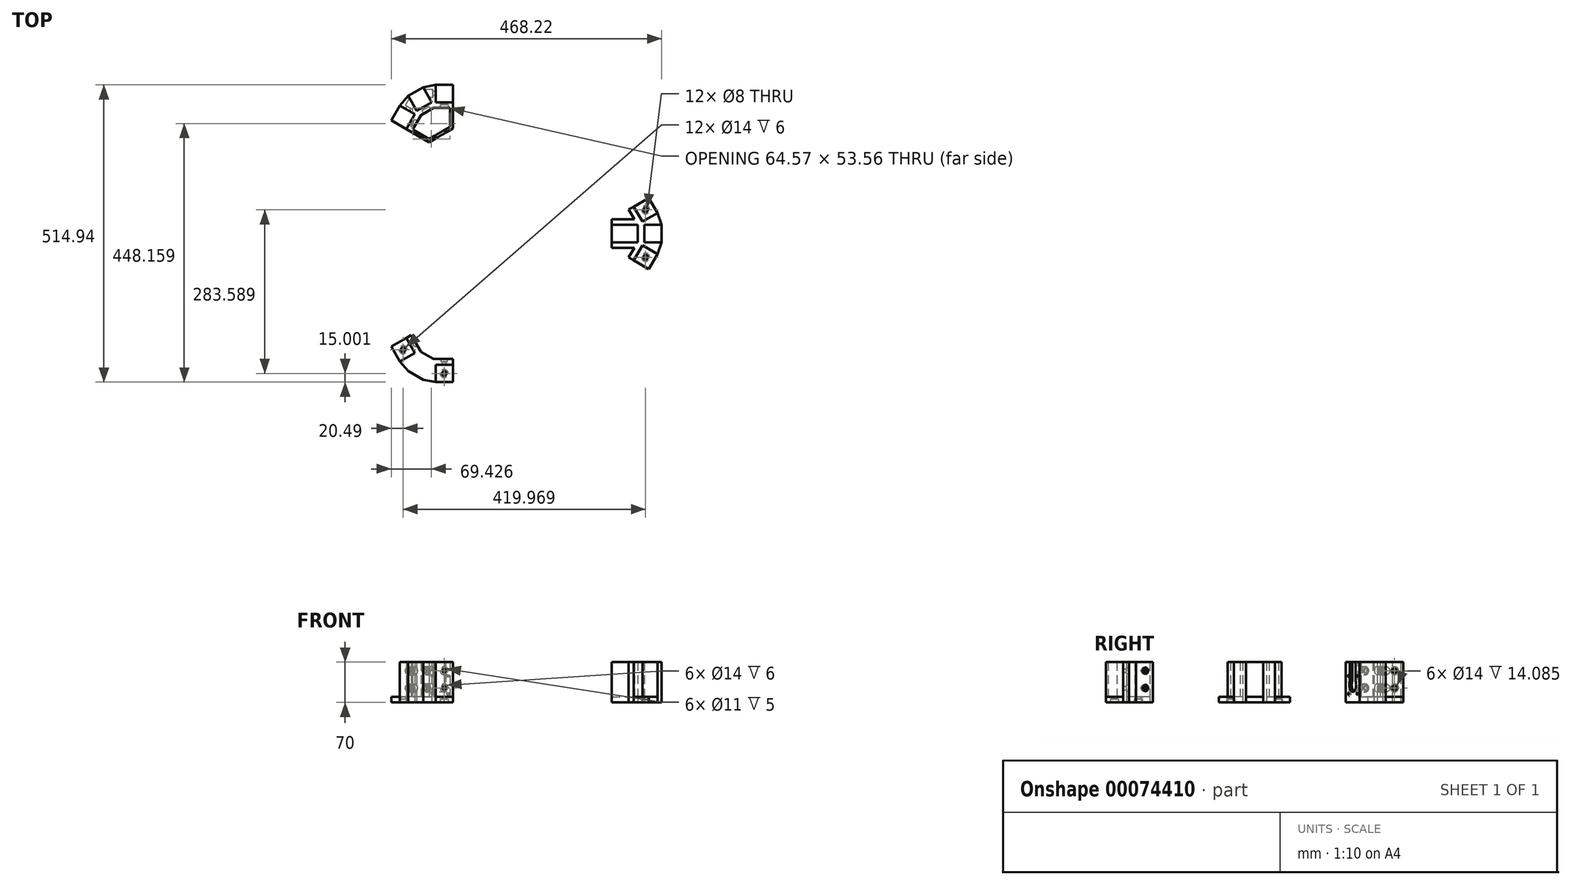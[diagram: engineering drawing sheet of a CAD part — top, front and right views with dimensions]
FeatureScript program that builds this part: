
annotation { "Feature Type Name" : "Feature", "Feature Type Description" : "" }
export const myFeature = defineFeature(function(context is Context, id is Id, definition is map)
    precondition{}
    {
        {
            var Q0;
            Q0=qCreatedBy(makeId("Top.planeOp"),FACE);
            var sketch = newSketch(context, id + "F0", { "sketchPlane" : qUnion([Q0])});
            skCircle(sketch, "E0", {"center": v(0, 0) * mm, "radius": 150 * mm, "construction": true});
            skCircle(sketch, "E1.cCircle", {"center": v(0, 0) * mm, "radius": 253.45 * mm, "construction": true});
            skLineSegment(sketch, "E1.0", {"start": v(-146.33, 253.45) * mm, "end": v(146.33, 253.45) * mm, "construction": true});
            skLineSegment(sketch, "E1.1", {"start": v(146.33, 253.45) * mm, "end": v(292.66, 0) * mm, "construction": true});
            skLineSegment(sketch, "E1.2", {"start": v(292.66, 0) * mm, "end": v(146.33, -253.45) * mm, "construction": true});
            skLineSegment(sketch, "E1.3", {"start": v(146.33, -253.45) * mm, "end": v(-146.33, -253.45) * mm, "construction": true});
            skLineSegment(sketch, "E1.4", {"start": v(-146.33, -253.45) * mm, "end": v(-292.66, 0) * mm, "construction": true});
            skLineSegment(sketch, "E1.5", {"start": v(-292.66, 0) * mm, "end": v(-146.33, 253.45) * mm, "construction": true});
            skPoint(sketch, "E1.0.midPoint", {"position": v(0, 253.45) * mm});
            skCircle(sketch, "E2.cCircle", {"center": v(0, 0) * mm, "radius": 284 * mm, "construction": true});
            skLineSegment(sketch, "E2.0", {"start": v(284, 163.97) * mm, "end": v(284, -163.97) * mm, "construction": true});
            skLineSegment(sketch, "E2.1", {"start": v(284, -163.97) * mm, "end": v(0, -327.93) * mm, "construction": true});
            skLineSegment(sketch, "E2.2", {"start": v(0, -327.93) * mm, "end": v(-284, -163.97) * mm, "construction": true});
            skLineSegment(sketch, "E2.3", {"start": v(-284, -163.97) * mm, "end": v(-284, 163.97) * mm, "construction": true});
            skLineSegment(sketch, "E2.4", {"start": v(-284, 163.97) * mm, "end": v(0, 327.93) * mm, "construction": true});
            skLineSegment(sketch, "E2.5", {"start": v(0, 327.93) * mm, "end": v(284, 163.97) * mm, "construction": true});
            skPoint(sketch, "E2.0.midPoint", {"position": v(284, 0) * mm});
            skLineSegment(sketch, "E3", {"start": v(-129, 253.45) * mm, "end": v(-154.99, 238.45) * mm});
            skLineSegment(sketch, "E4.0", {"start": v(-254, -146.65) * mm, "end": v(-254, 146.65) * mm, "construction": true});
            skLineSegment(sketch, "E4.1", {"start": v(0, 293.3) * mm, "end": v(254, 146.65) * mm, "construction": true});
            skLineSegment(sketch, "E4.2", {"start": v(254, 146.65) * mm, "end": v(254, -146.65) * mm, "construction": true});
            skLineSegment(sketch, "E4.3", {"start": v(-254, 146.65) * mm, "end": v(0, 293.3) * mm, "construction": true});
            skLineSegment(sketch, "E4.4", {"start": v(254, -146.65) * mm, "end": v(0, -293.3) * mm, "construction": true});
            skLineSegment(sketch, "E4.5", {"start": v(0, -293.3) * mm, "end": v(-254, -146.65) * mm, "construction": true});
            skLineSegment(sketch, "E5", {"start": v(-129, 253.45) * mm, "end": v(-114, 227.47) * mm});
            skLineSegment(sketch, "E6", {"start": v(-114, 227.47) * mm, "end": v(-139.99, 212.47) * mm});
            skLineSegment(sketch, "E7", {"start": v(-139.99, 212.47) * mm, "end": v(-154.99, 238.45) * mm});
            skLineSegment(sketch, "E8.0", {"start": v(-262.66, 0) * mm, "end": v(-131.33, 227.47) * mm, "construction": true});
            skLineSegment(sketch, "E8.1", {"start": v(131.33, 227.47) * mm, "end": v(262.66, 0) * mm, "construction": true});
            skLineSegment(sketch, "E8.2", {"start": v(262.66, 0) * mm, "end": v(131.33, -227.47) * mm, "construction": true});
            skLineSegment(sketch, "E8.3", {"start": v(-131.33, 227.47) * mm, "end": v(131.33, 227.47) * mm, "construction": true});
            skLineSegment(sketch, "E8.4", {"start": v(131.33, -227.47) * mm, "end": v(-131.33, -227.47) * mm, "construction": true});
            skLineSegment(sketch, "E8.5", {"start": v(-131.33, -227.47) * mm, "end": v(-262.66, 0) * mm, "construction": true});
            skLineSegment(sketch, "E9", {"start": v(-114, 227.47) * mm, "end": v(-107.5, 227.47) * mm});
            skLineSegment(sketch, "E10", {"start": v(-107.5, 227.47) * mm, "end": v(-77.5, 227.47) * mm});
            skLineSegment(sketch, "E11", {"start": v(-77.5, 227.47) * mm, "end": v(-77.5, 257.47) * mm});
            skLineSegment(sketch, "E12", {"start": v(-77.5, 257.47) * mm, "end": v(-107.5, 257.47) * mm});
            skLineSegment(sketch, "E13", {"start": v(-107.5, 257.47) * mm, "end": v(-129, 253.45) * mm});
            skLineSegment(sketch, "E14", {"start": v(-107.5, 227.47) * mm, "end": v(-107.5, 257.47) * mm});
            skLineSegment(sketch, "E15", {"start": v(-139.99, 212.47) * mm, "end": v(-143.24, 206.84) * mm});
            skLineSegment(sketch, "E16", {"start": v(-143.24, 206.84) * mm, "end": v(-158.24, 180.86) * mm});
            skLineSegment(sketch, "E17", {"start": v(-158.24, 180.86) * mm, "end": v(-184.22, 195.86) * mm});
            skLineSegment(sketch, "E18", {"start": v(-184.22, 195.86) * mm, "end": v(-169.22, 221.84) * mm});
            skLineSegment(sketch, "E19", {"start": v(-169.22, 221.84) * mm, "end": v(-154.99, 238.45) * mm});
            skLineSegment(sketch, "E20", {"start": v(-169.22, 221.84) * mm, "end": v(-143.24, 206.84) * mm});
            skLineSegment(sketch, "E21", {"start": v(-77.5, 227.47) * mm, "end": v(-77.5, 217.47) * mm});
            skLineSegment(sketch, "E22", {"start": v(-77.5, 217.47) * mm, "end": v(-111.33, 217.47) * mm});
            skLineSegment(sketch, "E23", {"start": v(-111.33, 217.47) * mm, "end": v(-132.67, 205.15) * mm});
            skLineSegment(sketch, "E24", {"start": v(-132.67, 205.15) * mm, "end": v(-149.58, 175.86) * mm});
            skLineSegment(sketch, "E25", {"start": v(-149.58, 175.86) * mm, "end": v(-158.24, 180.86) * mm});
            skLineSegment(sketch, "E26", {"start": v(-149.58, 175.86) * mm, "end": v(-118.88, 158.14) * mm});
            skLineSegment(sketch, "E27", {"start": v(-118.88, 158.14) * mm, "end": v(-77.5, 182.02) * mm});
            skLineSegment(sketch, "E28", {"start": v(-77.5, 182.02) * mm, "end": v(-77.5, 217.47) * mm});
            skLineSegment(sketch, "E29", {"start": v(-82.5, 184.9) * mm, "end": v(-118.88, 163.9) * mm});
            skLineSegment(sketch, "E30", {"start": v(-118.88, 163.9) * mm, "end": v(-147.08, 180.19) * mm});
            skLineSegment(sketch, "E31", {"start": v(-82.5, 184.9) * mm, "end": v(-82.5, 217.47) * mm});
            skLineSegment(sketch, "E32.1.0", {"start": v(-143.24, -206.84) * mm, "end": v(-169.22, -221.84) * mm});
            skLineSegment(sketch, "E32.1.1", {"start": v(-107.5, -257.47) * mm, "end": v(-107.5, -227.47) * mm});
            skLineSegment(sketch, "E32.1.2", {"start": v(-114, -227.47) * mm, "end": v(-129, -253.45) * mm});
            skLineSegment(sketch, "E32.1.3", {"start": v(-149.58, -175.86) * mm, "end": v(-132.67, -205.15) * mm});
            skLineSegment(sketch, "E32.1.4", {"start": v(-139.99, -212.47) * mm, "end": v(-114, -227.47) * mm});
            skLineSegment(sketch, "E32.1.5", {"start": v(-169.22, -221.84) * mm, "end": v(-154.99, -238.45) * mm});
            skLineSegment(sketch, "E32.1.6", {"start": v(-158.24, -180.86) * mm, "end": v(-184.22, -195.86) * mm});
            skLineSegment(sketch, "E32.1.7", {"start": v(-154.99, -238.45) * mm, "end": v(-129, -253.45) * mm});
            skLineSegment(sketch, "E32.1.8", {"start": v(-184.22, -195.86) * mm, "end": v(-169.22, -221.84) * mm});
            skLineSegment(sketch, "E32.1.9", {"start": v(-132.67, -205.15) * mm, "end": v(-111.33, -217.47) * mm});
            skLineSegment(sketch, "E32.1.10", {"start": v(-143.24, -206.84) * mm, "end": v(-158.24, -180.86) * mm});
            skLineSegment(sketch, "E32.1.11", {"start": v(-107.5, -257.47) * mm, "end": v(-129, -253.45) * mm});
            skLineSegment(sketch, "E32.1.12", {"start": v(-111.33, -217.47) * mm, "end": v(-77.5, -217.47) * mm});
            skLineSegment(sketch, "E32.1.13", {"start": v(-77.5, -257.47) * mm, "end": v(-107.5, -257.47) * mm});
            skLineSegment(sketch, "E32.1.14", {"start": v(-154.99, -238.45) * mm, "end": v(-139.99, -212.47) * mm});
            skLineSegment(sketch, "E32.1.15", {"start": v(-158.24, -180.86) * mm, "end": v(-149.58, -175.86) * mm});
            skLineSegment(sketch, "E32.1.16", {"start": v(-77.5, -227.47) * mm, "end": v(-77.5, -257.47) * mm});
            skLineSegment(sketch, "E32.1.17", {"start": v(-107.5, -227.47) * mm, "end": v(-77.5, -227.47) * mm});
            skLineSegment(sketch, "E32.1.18", {"start": v(-114, -227.47) * mm, "end": v(-107.5, -227.47) * mm});
            skLineSegment(sketch, "E32.1.19", {"start": v(-139.99, -212.47) * mm, "end": v(-143.24, -206.84) * mm});
            skLineSegment(sketch, "E32.1.20", {"start": v(-77.5, -217.47) * mm, "end": v(-77.5, -227.47) * mm});
            skLineSegment(sketch, "E32.2.0", {"start": v(250.75, -20.63) * mm, "end": v(276.73, -35.63) * mm});
            skLineSegment(sketch, "E32.2.1", {"start": v(276.73, 35.63) * mm, "end": v(250.75, 20.63) * mm});
            skLineSegment(sketch, "E32.2.2", {"start": v(254, 15) * mm, "end": v(284, 15) * mm});
            skLineSegment(sketch, "E32.2.3", {"start": v(227.09, -41.6) * mm, "end": v(244, -12.32) * mm});
            skLineSegment(sketch, "E32.2.4", {"start": v(254, -15) * mm, "end": v(254, 15) * mm});
            skLineSegment(sketch, "E32.2.5", {"start": v(276.73, -35.63) * mm, "end": v(284, -15) * mm});
            skLineSegment(sketch, "E32.2.6", {"start": v(235.75, -46.6) * mm, "end": v(261.73, -61.6) * mm});
            skLineSegment(sketch, "E32.2.7", {"start": v(284, -15) * mm, "end": v(284, 15) * mm});
            skLineSegment(sketch, "E32.2.8", {"start": v(261.73, -61.6) * mm, "end": v(276.73, -35.63) * mm});
            skLineSegment(sketch, "E32.2.10", {"start": v(250.75, -20.63) * mm, "end": v(235.75, -46.6) * mm});
            skLineSegment(sketch, "E32.2.11", {"start": v(276.73, 35.63) * mm, "end": v(284, 15) * mm});
            skLineSegment(sketch, "E32.2.12", {"start": v(244, 12.32) * mm, "end": v(227.09, 41.6) * mm});
            skLineSegment(sketch, "E32.2.13", {"start": v(261.73, 61.6) * mm, "end": v(276.73, 35.63) * mm});
            skLineSegment(sketch, "E32.2.14", {"start": v(284, -15) * mm, "end": v(254, -15) * mm});
            skLineSegment(sketch, "E32.2.15", {"start": v(235.75, -46.6) * mm, "end": v(227.09, -41.6) * mm});
            skLineSegment(sketch, "E32.2.16", {"start": v(235.75, 46.6) * mm, "end": v(261.73, 61.6) * mm});
            skLineSegment(sketch, "E32.2.17", {"start": v(250.75, 20.63) * mm, "end": v(235.75, 46.6) * mm});
            skLineSegment(sketch, "E32.2.18", {"start": v(254, 15) * mm, "end": v(250.75, 20.63) * mm});
            skLineSegment(sketch, "E32.2.19", {"start": v(254, -15) * mm, "end": v(250.75, -20.63) * mm});
            skLineSegment(sketch, "E32.2.20", {"start": v(227.09, 41.6) * mm, "end": v(235.75, 46.6) * mm});
            skLineSegment(sketch, "E33", {"start": v(254, 15) * mm, "end": v(242.45, 15) * mm, "construction": true});
            skLineSegment(sketch, "E34", {"start": v(254, -15) * mm, "end": v(242.45, -15) * mm, "construction": true});
            skLineSegment(sketch, "E35", {"start": v(242.45, -15) * mm, "end": v(197.45, -15) * mm});
            skLineSegment(sketch, "E36", {"start": v(197.45, -15) * mm, "end": v(197.45, 15) * mm});
            skLineSegment(sketch, "E37", {"start": v(197.45, 15) * mm, "end": v(242.45, 15) * mm});
            skLineSegment(sketch, "E38", {"start": v(242.45, -15) * mm, "end": v(242.45, 15) * mm});
            skLineSegment(sketch, "E39", {"start": v(236.68, 25) * mm, "end": v(197.45, 25) * mm});
            skLineSegment(sketch, "E40", {"start": v(197.45, 25) * mm, "end": v(197.45, 15) * mm});
            skLineSegment(sketch, "E41", {"start": v(236.68, -25) * mm, "end": v(197.45, -25) * mm});
            skLineSegment(sketch, "E42", {"start": v(197.45, -25) * mm, "end": v(197.45, -15) * mm});
            skLineSegment(sketch, "E43", {"start": v(-77.5, -257.47) * mm, "end": v(-107.5, -227.47) * mm, "construction": true});
            skLineSegment(sketch, "E44", {"start": v(-143.24, -206.84) * mm, "end": v(-184.22, -195.86) * mm, "construction": true});
            skPoint(sketch, "E45", {"position": v(-92.5, -242.47) * mm});
            skPoint(sketch, "E46", {"position": v(-163.73, -201.35) * mm});
            skLineSegment(sketch, "E47", {"start": v(235.75, -46.6) * mm, "end": v(276.73, -35.63) * mm, "construction": true});
            skLineSegment(sketch, "E48", {"start": v(250.75, 20.63) * mm, "end": v(261.73, 61.6) * mm, "construction": true});
            skPoint(sketch, "E49", {"position": v(256.24, -41.12) * mm});
            skPoint(sketch, "E50", {"position": v(256.24, 41.12) * mm});
            skSolve(sketch);
        }
        {
            var Q0;
            Q0=makeQuery(id+"F0.imprint","IMPRINT",FACE,{"disambiguationData":[TD([[makeQuery(id+"F0.imprint","IMPRINT",EDGE,{"derivedFrom":sQuery(id+"F0.wireOp",EDGE,"b67b0f4b-a2f8-46fb-98a8-05c8234a12aa.1.1")}),-1.0]])]});
            var Q1;
            Q1=makeQuery(id+"F0.imprint","IMPRINT",FACE,{"disambiguationData":[TD([[makeQuery(id+"F0.imprint","IMPRINT",EDGE,{"derivedFrom":sQuery(id+"F0.wireOp",EDGE,"b67b0f4b-a2f8-46fb-98a8-05c8234a12aa.1.4")}),1.0]])]});
            var Q2;
            Q2=makeQuery(id+"F0.imprint","IMPRINT",FACE,{"disambiguationData":[TD([[makeQuery(id+"F0.imprint","IMPRINT",EDGE,{"derivedFrom":sQuery(id+"F0.wireOp",EDGE,"b67b0f4b-a2f8-46fb-98a8-05c8234a12aa.1.5")}),1.0]])]});
            var Q3;
            {var subQ0=sQuery(id+"F0.wireOp",EDGE,"4VLoyTS8-C0T2-iWtc-Nw30-vaCpkBEcr5Km");Q3=makeQuery(id+"F0.imprint","IMPRINT",FACE,{"disambiguationData":[TD([[makeQuery(id+"F0.imprint","IMPRINT",EDGE,{"derivedFrom":subQ0}),1.0]])]});}
            var Q4;
            {var subQ0=sQuery(id+"F0.wireOp",EDGE,"xXZ7WPOc-jZ2e-64wJ-Mn5F-6zut2eX6ouj1");Q4=makeQuery(id+"F0.imprint","IMPRINT",FACE,{"disambiguationData":[TD([[makeQuery(id+"F0.imprint","IMPRINT",EDGE,{"derivedFrom":subQ0}),1.0]])]});}
            var Q5;
            Q5=makeQuery(id+"F0.imprint","IMPRINT",FACE,{"disambiguationData":[TD([[makeQuery(id+"F0.imprint","IMPRINT",EDGE,{"derivedFrom":sQuery(id+"F0.wireOp",EDGE,"b67b0f4b-a2f8-46fb-98a8-05c8234a12aa.2.5")}),1.0]])]});
            var Q6;
            Q6=makeQuery(id+"F0.imprint","IMPRINT",FACE,{"disambiguationData":[TD([[makeQuery(id+"F0.imprint","IMPRINT",EDGE,{"derivedFrom":sQuery(id+"F0.wireOp",EDGE,"b67b0f4b-a2f8-46fb-98a8-05c8234a12aa.2.1")}),-1.0]])]});
            var Q7;
            Q7=makeQuery(id+"F0.imprint","IMPRINT",FACE,{"disambiguationData":[TD([[makeQuery(id+"F0.imprint","IMPRINT",EDGE,{"derivedFrom":sQuery(id+"F0.wireOp",EDGE,"b67b0f4b-a2f8-46fb-98a8-05c8234a12aa.2.0")}),1.0]])]});
            var Q8;
            Q8=makeQuery(id+"F0.imprint","IMPRINT",FACE,{"disambiguationData":[TD([[makeQuery(id+"F0.imprint","IMPRINT",EDGE,{"derivedFrom":sQuery(id+"F0.wireOp",EDGE,"b67b0f4b-a2f8-46fb-98a8-05c8234a12aa.2.4")}),1.0]])]});
            var Q9;
            {var subQ0=sQuery(id+"F0.wireOp",EDGE,"E26");Q9=makeQuery(id+"F0.imprint","IMPRINT",FACE,{"disambiguationData":[TD([[makeQuery(id+"F0.imprint","IMPRINT",EDGE,{"derivedFrom":subQ0}),1.0]])]});}
            var Q10;
            Q10=makeQuery(id+"F0.imprint","IMPRINT",FACE,{"disambiguationData":[TD([[makeQuery(id+"F0.imprint","IMPRINT",EDGE,{"derivedFrom":sQuery(id+"F0.wireOp",EDGE,"E6")}),1.0]])]});
            var Q11;
            Q11=makeQuery(id+"F0.imprint","IMPRINT",FACE,{"disambiguationData":[TD([[makeQuery(id+"F0.imprint","IMPRINT",EDGE,{"derivedFrom":sQuery(id+"F0.wireOp",EDGE,"E5")}),1.0]])]});
            var Q12;
            Q12=makeQuery(id+"F0.imprint","IMPRINT",FACE,{"disambiguationData":[TD([[makeQuery(id+"F0.imprint","IMPRINT",EDGE,{"derivedFrom":sQuery(id+"F0.wireOp",EDGE,"E7")}),1.0]])]});
            extrude(context, id + "F1", {"entities" : qUnion([Q0, Q1, Q2, Q3, Q4, Q5, Q6, Q7, Q8, Q9, Q10, Q11, Q12]), "depth" : 70 * mm});
        }
        {
            var Q0;
            Q0=makeQuery(id+"F0.imprint","IMPRINT",FACE,{"disambiguationData":[TD([[makeQuery(id+"F0.imprint","IMPRINT",EDGE,{"derivedFrom":sQuery(id+"F0.wireOp",EDGE,"b67b0f4b-a2f8-46fb-98a8-05c8234a12aa.1.2")}),-1.0]])]});
            var Q1;
            Q1=makeQuery(id+"F0.imprint","IMPRINT",FACE,{"disambiguationData":[TD([[makeQuery(id+"F0.imprint","IMPRINT",EDGE,{"derivedFrom":sQuery(id+"F0.wireOp",EDGE,"E16")}),-1.0]])]});
            var Q2;
            Q2=makeQuery(id+"F0.imprint","IMPRINT",FACE,{"disambiguationData":[TD([[makeQuery(id+"F0.imprint","IMPRINT",EDGE,{"derivedFrom":sQuery(id+"F0.wireOp",EDGE,"E3")}),1.0]])]});
            var Q3;
            Q3=makeQuery(id+"F0.imprint","IMPRINT",FACE,{"disambiguationData":[TD([[makeQuery(id+"F0.imprint","IMPRINT",EDGE,{"derivedFrom":sQuery(id+"F0.wireOp",EDGE,"E10")}),1.0]])]});
            var Q4;
            Q4=makeQuery(id+"F0.imprint","IMPRINT",FACE,{"disambiguationData":[TD([[makeQuery(id+"F0.imprint","IMPRINT",EDGE,{"derivedFrom":sQuery(id+"F0.wireOp",EDGE,"b67b0f4b-a2f8-46fb-98a8-05c8234a12aa.1.0")}),1.0]])]});
            var Q5;
            Q5=makeQuery(id+"F0.imprint","IMPRINT",FACE,{"disambiguationData":[TD([[makeQuery(id+"F0.imprint","IMPRINT",EDGE,{"derivedFrom":sQuery(id+"F0.wireOp",EDGE,"b67b0f4b-a2f8-46fb-98a8-05c8234a12aa.1.4")}),-1.0]])]});
            var Q6;
            Q6=makeQuery(id+"F0.imprint","IMPRINT",FACE,{"disambiguationData":[TD([[makeQuery(id+"F0.imprint","IMPRINT",EDGE,{"derivedFrom":sQuery(id+"F0.wireOp",EDGE,"b67b0f4b-a2f8-46fb-98a8-05c8234a12aa.2.4")}),-1.0]])]});
            var Q7;
            Q7=makeQuery(id+"F0.imprint","IMPRINT",FACE,{"disambiguationData":[TD([[makeQuery(id+"F0.imprint","IMPRINT",EDGE,{"derivedFrom":sQuery(id+"F0.wireOp",EDGE,"c2546d1c-4651-43b4-96d7-ae65259f8c30.1.7")}),1.0]])]});
            var Q8;
            Q8=makeQuery(id+"F0.imprint","IMPRINT",FACE,{"disambiguationData":[TD([[makeQuery(id+"F0.imprint","IMPRINT",EDGE,{"derivedFrom":sQuery(id+"F0.wireOp",EDGE,"b67b0f4b-a2f8-46fb-98a8-05c8234a12aa.2.2")}),-1.0]])]});
            extrude(context, id + "F2", {"entities" : qUnion([Q0, Q1, Q2, Q3, Q4, Q5, Q6, Q7, Q8]), "depth" : 10 * mm});
        }
        {
            var Q0;
            Q0=makeQuery(id+"F1.opExtrude","SWEPT_FACE",FACE,{"disambiguationData":[OSD([sQuery(id+"F0.wireOp",EDGE,"E27")])]});
            var sketch = newSketch(context, id + "F3", { "sketchPlane" : qUnion([Q0])});
            skLineSegment(sketch, "E51", {"start": v(0, 70) * mm, "end": v(0, 0) * mm, "construction": true});
            skLineSegment(sketch, "E52.0", {"start": v(-15.5, 70) * mm, "end": v(-15.5, -5) * mm, "construction": true});
            skLineSegment(sketch, "E53.0", {"start": v(15.5, 70) * mm, "end": v(15.5, -5) * mm, "construction": true});
            skLineSegment(sketch, "E54.0", {"start": v(-23.89, 15) * mm, "end": v(23.89, 15) * mm, "construction": true});
            skLineSegment(sketch, "E55.0", {"start": v(-23.89, 46) * mm, "end": v(23.89, 46) * mm, "construction": true});
            skLineSegment(sketch, "E56.0", {"start": v(10, 70) * mm, "end": v(10, -5) * mm, "construction": true});
            skLineSegment(sketch, "E57.0", {"start": v(-10, 70) * mm, "end": v(-10, -5) * mm, "construction": true});
            skLineSegment(sketch, "E58", {"start": v(-15.5, 46) * mm, "end": v(15.5, 15) * mm, "construction": true});
            skLineSegment(sketch, "E59", {"start": v(-15.5, 15) * mm, "end": v(15.5, 46) * mm, "construction": true});
            skCircle(sketch, "E60", {"center": v(0, 30.5) * mm, "radius": 12 * mm});
            skLineSegment(sketch, "E61", {"start": v(-10, 37.13) * mm, "end": v(-10, 70) * mm});
            skLineSegment(sketch, "E62", {"start": v(10, 37.13) * mm, "end": v(10, 70) * mm});
            skSolve(sketch);
        }
        {
            var Q0;
            {var subQ0=sQuery(id+"F3.wireOp",EDGE,"E60");var subQ1=makeQuery(id+"F3.imprint","INTERSECT",VERTEX,{"derivedFrom":[subQ0,sQuery(id+"F3.wireOp",EDGE,"E61")]});Q0=makeQuery(id+"F3.imprint","IMPRINT",FACE,{"disambiguationData":[TD([[makeQuery(id+"F3.imprint","IMPRINT",EDGE,{"disambiguationData":[TD([[subQ1,1.0]])],"derivedFrom":subQ0}),1.0]])]});}
            var Q1;
            {var subQ0=sQuery(id+"F3.wireOp",EDGE,"E61");Q1=makeQuery(id+"F3.imprint","IMPRINT",FACE,{"disambiguationData":[TD([[makeQuery(id+"F3.imprint","IMPRINT",EDGE,{"derivedFrom":subQ0}),-1.0]])]});}
            extrude(context, id + "F4", {"entities" : qUnion([Q0, Q1]), "operationType" : NewBodyOperationType.REMOVE, "oppositeDirection" : true, "depth" : 25 * mm});
        }
        {
            var Q0;
            Q0=makeQuery(id+"F4.boolean.opBoolean","COPY",EDGE,{"derivedFrom":makeQuery(id+"F4.opExtrude","SWEPT_EDGE",EDGE,{"disambiguationData":[OSD([sQuery(id+"F0.wireOp",EDGE,"E27"),sQuery(id+"F3.wireOp",EDGE,"E61")])]})});
            var Q1;
            Q1=makeQuery(id+"F4.boolean.opBoolean","COPY",EDGE,{"derivedFrom":makeQuery(id+"F4.opExtrude","SWEPT_EDGE",EDGE,{"disambiguationData":[OSD([sQuery(id+"F0.wireOp",EDGE,"E27"),sQuery(id+"F3.wireOp",EDGE,"E62")])]})});
            var Q2;
            Q2=makeQuery(id+"F4.boolean.opBoolean","COPY",EDGE,{"derivedFrom":makeQuery(id+"F4.opExtrude","SWEPT_EDGE",EDGE,{"disambiguationData":[OSD([sQuery(id+"F3.wireOp",EDGE,"E60"),sQuery(id+"F3.wireOp",EDGE,"E61")])]})});
            var Q3;
            Q3=makeQuery(id+"F4.boolean.opBoolean","COPY",EDGE,{"derivedFrom":makeQuery(id+"F4.opExtrude","SWEPT_EDGE",EDGE,{"disambiguationData":[OSD([sQuery(id+"F3.wireOp",EDGE,"E60"),sQuery(id+"F3.wireOp",EDGE,"E62")])]})});
            fillet(context, id + "F5", {"entities" : qUnion([Q0, Q1, Q2, Q3]), "radius" : 10 * mm, "tangentPropagation" : true, "allowEdgeOverflow" : false});
        }
        {
            var Q0;
            Q0=makeQuery(id+"F1.opExtrude","SWEPT_FACE",FACE,{"disambiguationData":[OSD([sQuery(id+"F0.wireOp",EDGE,"E23")])]});
            var sketch = newSketch(context, id + "F6", { "sketchPlane" : qUnion([Q0])});
            skLineSegment(sketch, "E63", {"start": v(0, 0) * mm, "end": v(0, 70) * mm, "construction": true});
            skLineSegment(sketch, "E64", {"start": v(0, 70) * mm, "end": v(0, 55) * mm, "construction": true});
            skLineSegment(sketch, "E65", {"start": v(0, 55) * mm, "end": v(0, 25) * mm, "construction": true});
            skSolve(sketch);
        }
        {
            var Q0;
            Q0=makeQuery(id+"F1.opExtrude","CAP_FACE",FACE,{"disambiguationData":[OSD([sQuery(id+"F0.wireOp",EDGE,"E5"),sQuery(id+"F0.wireOp",EDGE,"E6"),sQuery(id+"F0.wireOp",EDGE,"E7"),sQuery(id+"F0.wireOp",EDGE,"E10"),sQuery(id+"F0.wireOp",EDGE,"E13"),sQuery(id+"F0.wireOp",EDGE,"E14"),sQuery(id+"F0.wireOp",EDGE,"E16"),sQuery(id+"F0.wireOp",EDGE,"E19"),sQuery(id+"F0.wireOp",EDGE,"E20"),sQuery(id+"F0.wireOp",EDGE,"E21"),sQuery(id+"F0.wireOp",EDGE,"E22"),sQuery(id+"F0.wireOp",EDGE,"E23"),sQuery(id+"F0.wireOp",EDGE,"E24"),sQuery(id+"F0.wireOp",EDGE,"E25"),sQuery(id+"F0.wireOp",EDGE,"E26"),sQuery(id+"F0.wireOp",EDGE,"E27"),sQuery(id+"F0.wireOp",EDGE,"E28"),sQuery(id+"F0.wireOp",EDGE,"E29"),sQuery(id+"F0.wireOp",EDGE,"E30"),sQuery(id+"F0.wireOp",EDGE,"E31")])],"isStart":false});
            var sketch = newSketch(context, id + "F7", { "sketchPlane" : qUnion([Q0])});
            skLineSegment(sketch, "E66", {"start": v(-107.5, 242.47) * mm, "end": v(-122.67, 242.47) * mm, "construction": true});
            skLineSegment(sketch, "E67", {"start": v(-122.67, 242.47) * mm, "end": v(-148.65, 227.47) * mm, "construction": true});
            skLineSegment(sketch, "E68", {"start": v(-148.65, 227.47) * mm, "end": v(-156.23, 214.34) * mm, "construction": true});
            skLineSegment(sketch, "E69", {"start": v(-129, 253.45) * mm, "end": v(-107.5, 253.45) * mm, "construction": true});
            skLineSegment(sketch, "E70", {"start": v(-154.99, 238.45) * mm, "end": v(-165.74, 219.83) * mm, "construction": true});
            skLineSegment(sketch, "E71", {"start": v(-107.5, 253.45) * mm, "end": v(-107.5, 242.47) * mm, "construction": true});
            skLineSegment(sketch, "E72", {"start": v(-156.23, 214.34) * mm, "end": v(-165.74, 219.83) * mm, "construction": true});
            skSolve(sketch);
        }
        {
            var Q0;
            Q0=makeQuery(id+"F1.opExtrude","SWEPT_FACE",FACE,{"disambiguationData":[OSD([sQuery(id+"F0.wireOp",EDGE,"E14")])]});
            var Q1;
            Q1=sQuery(id+"F7.wireOp",VERTEX,"E69.start");
            cPlane(context, id + "F8", {"entities" : qUnion([Q0, Q1]), "cplaneType" : CPlaneType.PLANE_POINT, "offset" : 150 * mm, "width" : 150 * mm, "height" : 150 * mm});
        }
        {
            var Q0;
            Q0=qCreatedBy(id+"F8.planeOp",FACE);
            var sketch = newSketch(context, id + "F9", { "sketchPlane" : qUnion([Q0])});
            skLineSegment(sketch, "E73.0", {"start": v(242.47, 70) * mm, "end": v(242.47, 0) * mm, "construction": true});
            skPoint(sketch, "E74", {"position": v(242.47, 55) * mm});
            skPoint(sketch, "E75", {"position": v(242.47, 25) * mm});
            skSolve(sketch);
        }
        {
            var Q0;
            Q0=makeQuery(id+"F1.opExtrude","SWEPT_FACE",FACE,{"disambiguationData":[OSD([sQuery(id+"F0.wireOp",EDGE,"E20")])]});
            var Q1;
            Q1=sQuery(id+"F7.wireOp",VERTEX,"E70.start");
            cPlane(context, id + "F10", {"entities" : qUnion([Q0, Q1]), "cplaneType" : CPlaneType.PLANE_POINT, "offset" : 150 * mm, "width" : 150 * mm, "height" : 150 * mm});
        }
        {
            var Q0;
            Q0=qCreatedBy(id+"F10.planeOp",FACE);
            var sketch = newSketch(context, id + "F11", { "sketchPlane" : qUnion([Q0])});
            skLineSegment(sketch, "E76.0", {"start": v(-242.47, 70) * mm, "end": v(-242.47, 0) * mm, "construction": true});
            skPoint(sketch, "E77", {"position": v(-242.47, 55) * mm});
            skPoint(sketch, "E78", {"position": v(-242.47, 25) * mm});
            skSolve(sketch);
        }
        {
            var Q0;
            Q0=makeQuery(id+"F1.opExtrude","SWEPT_FACE",FACE,{"disambiguationData":[OSD([sQuery(id+"F0.wireOp",EDGE,"E24")])]});
            var sketch = newSketch(context, id + "F12", { "sketchPlane" : qUnion([Q0])});
            skLineSegment(sketch, "E79.0", {"start": v(92.5, 70) * mm, "end": v(92.5, 0) * mm, "construction": true});
            skPoint(sketch, "E80", {"position": v(92.5, 55) * mm});
            skPoint(sketch, "E81", {"position": v(92.5, 25) * mm});
            skSolve(sketch);
        }
        {
            var Q0;
            Q0=makeQuery(id+"F1.opExtrude","SWEPT_FACE",FACE,{"disambiguationData":[OSD([sQuery(id+"F0.wireOp",EDGE,"E22")])]});
            var sketch = newSketch(context, id + "F13", { "sketchPlane" : qUnion([Q0])});
            skLineSegment(sketch, "E82.0", {"start": v(-92.5, 70) * mm, "end": v(-92.5, 0) * mm, "construction": true});
            skPoint(sketch, "E83", {"position": v(-92.5, 55) * mm});
            skPoint(sketch, "E84", {"position": v(-92.5, 25) * mm});
            skSolve(sketch);
        }
        {
            var Q0;
            Q0=sQuery(id+"F3.wireOp",VERTEX,"E58.start");
            var Q1;
            Q1=sQuery(id+"F3.wireOp",VERTEX,"E59.end");
            var Q2;
            Q2=sQuery(id+"F3.wireOp",VERTEX,"E58.end");
            var Q3;
            Q3=sQuery(id+"F3.wireOp",VERTEX,"E59.start");
            var Q4;
            Q4=makeQuery(id+"F1.opExtrude","SWEPT_BODY",BODY,{"disambiguationData":[OSD([sQuery(id+"F0.wireOp",EDGE,"E5"),sQuery(id+"F0.wireOp",EDGE,"E6"),sQuery(id+"F0.wireOp",EDGE,"E7"),sQuery(id+"F0.wireOp",EDGE,"E10"),sQuery(id+"F0.wireOp",EDGE,"E13"),sQuery(id+"F0.wireOp",EDGE,"E14"),sQuery(id+"F0.wireOp",EDGE,"E16"),sQuery(id+"F0.wireOp",EDGE,"E19"),sQuery(id+"F0.wireOp",EDGE,"E20"),sQuery(id+"F0.wireOp",EDGE,"E21"),sQuery(id+"F0.wireOp",EDGE,"E22"),sQuery(id+"F0.wireOp",EDGE,"E23"),sQuery(id+"F0.wireOp",EDGE,"E24"),sQuery(id+"F0.wireOp",EDGE,"E25"),sQuery(id+"F0.wireOp",EDGE,"E26"),sQuery(id+"F0.wireOp",EDGE,"E27"),sQuery(id+"F0.wireOp",EDGE,"E28"),sQuery(id+"F0.wireOp",EDGE,"E29"),sQuery(id+"F0.wireOp",EDGE,"E30"),sQuery(id+"F0.wireOp",EDGE,"E31")])]});
            hole(context, id + "F14", {"style" : HoleStyle.SIMPLE, "holeDiameter" : 3 * mm, "endStyle" : HoleEndStyle.BLIND, "holeDepth" : 20 * mm, "locations" : qUnion([Q0, Q1, Q2, Q3]), "scope" : qUnion([Q4])});
        }
        {
            var Q0;
            Q0=sQuery(id+"F6.wireOp",VERTEX,"E65.start");
            var Q1;
            Q1=sQuery(id+"F6.wireOp",VERTEX,"E65.end");
            var Q2;
            Q2=sQuery(id+"F12.wireOp",VERTEX,"E80");
            var Q3;
            Q3=sQuery(id+"F12.wireOp",VERTEX,"E81");
            var Q4;
            Q4=sQuery(id+"F13.wireOp",VERTEX,"E84");
            var Q5;
            Q5=sQuery(id+"F13.wireOp",VERTEX,"E83");
            var Q6;
            Q6=makeQuery(id+"F1.opExtrude","SWEPT_BODY",BODY,{"disambiguationData":[OSD([sQuery(id+"F0.wireOp",EDGE,"E5"),sQuery(id+"F0.wireOp",EDGE,"E6"),sQuery(id+"F0.wireOp",EDGE,"E7"),sQuery(id+"F0.wireOp",EDGE,"E10"),sQuery(id+"F0.wireOp",EDGE,"E13"),sQuery(id+"F0.wireOp",EDGE,"E14"),sQuery(id+"F0.wireOp",EDGE,"E16"),sQuery(id+"F0.wireOp",EDGE,"E19"),sQuery(id+"F0.wireOp",EDGE,"E20"),sQuery(id+"F0.wireOp",EDGE,"E21"),sQuery(id+"F0.wireOp",EDGE,"E22"),sQuery(id+"F0.wireOp",EDGE,"E23"),sQuery(id+"F0.wireOp",EDGE,"E24"),sQuery(id+"F0.wireOp",EDGE,"E25"),sQuery(id+"F0.wireOp",EDGE,"E26"),sQuery(id+"F0.wireOp",EDGE,"E27"),sQuery(id+"F0.wireOp",EDGE,"E28"),sQuery(id+"F0.wireOp",EDGE,"E29"),sQuery(id+"F0.wireOp",EDGE,"E30"),sQuery(id+"F0.wireOp",EDGE,"E31")])]});
            hole(context, id + "F15", {"style" : HoleStyle.C_BORE, "holeDiameter" : 8 * mm, "cBoreDiameter" : 14 * mm, "cBoreDepth" : 6 * mm, "endStyle" : HoleEndStyle.THROUGH, "locations" : qUnion([Q0, Q1, Q2, Q3, Q4, Q5]), "scope" : qUnion([Q6])});
        }
        {
            var Q0;
            Q0=sQuery(id+"F9.wireOp",VERTEX,"E75");
            var Q1;
            Q1=sQuery(id+"F9.wireOp",VERTEX,"E74");
            var Q2;
            Q2=sQuery(id+"F11.wireOp",VERTEX,"E77");
            var Q3;
            Q3=sQuery(id+"F11.wireOp",VERTEX,"E78");
            var Q4;
            Q4=makeQuery(id+"F1.opExtrude","SWEPT_BODY",BODY,{"disambiguationData":[OSD([sQuery(id+"F0.wireOp",EDGE,"E5"),sQuery(id+"F0.wireOp",EDGE,"E6"),sQuery(id+"F0.wireOp",EDGE,"E7"),sQuery(id+"F0.wireOp",EDGE,"E10"),sQuery(id+"F0.wireOp",EDGE,"E13"),sQuery(id+"F0.wireOp",EDGE,"E14"),sQuery(id+"F0.wireOp",EDGE,"E16"),sQuery(id+"F0.wireOp",EDGE,"E19"),sQuery(id+"F0.wireOp",EDGE,"E20"),sQuery(id+"F0.wireOp",EDGE,"E21"),sQuery(id+"F0.wireOp",EDGE,"E22"),sQuery(id+"F0.wireOp",EDGE,"E23"),sQuery(id+"F0.wireOp",EDGE,"E24"),sQuery(id+"F0.wireOp",EDGE,"E25"),sQuery(id+"F0.wireOp",EDGE,"E26"),sQuery(id+"F0.wireOp",EDGE,"E27"),sQuery(id+"F0.wireOp",EDGE,"E28"),sQuery(id+"F0.wireOp",EDGE,"E29"),sQuery(id+"F0.wireOp",EDGE,"E30"),sQuery(id+"F0.wireOp",EDGE,"E31")])]});
            hole(context, id + "F16", {"style" : HoleStyle.C_BORE, "holeDiameter" : 8 * mm, "cBoreDiameter" : 14 * mm, "cBoreDepth" : 6 * mm, "endStyle" : HoleEndStyle.THROUGH, "oppositeDirection" : true, "locations" : qUnion([Q0, Q1, Q2, Q3]), "scope" : qUnion([Q4])});
        }
        {
            var Q0;
            Q0=makeQuery(id+"F0.imprint","IMPRINT",FACE,{"disambiguationData":[TD([[makeQuery(id+"F0.imprint","IMPRINT",EDGE,{"derivedFrom":sQuery(id+"F0.wireOp",EDGE,"E32.2.0")}),-1.0]])]});
            var Q1;
            Q1=makeQuery(id+"F0.imprint","IMPRINT",FACE,{"disambiguationData":[TD([[makeQuery(id+"F0.imprint","IMPRINT",EDGE,{"derivedFrom":sQuery(id+"F0.wireOp",EDGE,"E32.2.2")}),-1.0]])]});
            var Q2;
            Q2=makeQuery(id+"F0.imprint","IMPRINT",FACE,{"disambiguationData":[TD([[makeQuery(id+"F0.imprint","IMPRINT",EDGE,{"derivedFrom":sQuery(id+"F0.wireOp",EDGE,"E32.2.1")}),-1.0]])]});
            var Q3;
            Q3=makeQuery(id+"F0.imprint","IMPRINT",FACE,{"disambiguationData":[TD([[makeQuery(id+"F0.imprint","IMPRINT",EDGE,{"derivedFrom":sQuery(id+"F0.wireOp",EDGE,"E35")}),-1.0]])]});
            extrude(context, id + "F17", {"entities" : qUnion([Q0, Q1, Q2, Q3]), "depth" : 10 * mm});
        }
        {
            var Q0;
            Q0=makeQuery(id+"F0.imprint","IMPRINT",FACE,{"disambiguationData":[TD([[makeQuery(id+"F0.imprint","IMPRINT",EDGE,{"derivedFrom":sQuery(id+"F0.wireOp",EDGE,"E32.2.1")}),1.0]])]});
            var Q1;
            Q1=makeQuery(id+"F0.imprint","IMPRINT",FACE,{"disambiguationData":[TD([[makeQuery(id+"F0.imprint","IMPRINT",EDGE,{"derivedFrom":sQuery(id+"F0.wireOp",EDGE,"E32.2.0")}),1.0]])]});
            var Q2;
            Q2=makeQuery(id+"F0.imprint","IMPRINT",FACE,{"disambiguationData":[TD([[makeQuery(id+"F0.imprint","IMPRINT",EDGE,{"derivedFrom":sQuery(id+"F0.wireOp",EDGE,"E32.2.4")}),1.0]])]});
            var Q3;
            {var subQ0=sQuery(id+"F0.wireOp",EDGE,"E35");Q3=makeQuery(id+"F0.imprint","IMPRINT",FACE,{"disambiguationData":[TD([[makeQuery(id+"F0.imprint","IMPRINT",EDGE,{"derivedFrom":subQ0}),1.0]])]});}
            var Q4;
            {var subQ0=sQuery(id+"F0.wireOp",EDGE,"E37");Q4=makeQuery(id+"F0.imprint","IMPRINT",FACE,{"disambiguationData":[TD([[makeQuery(id+"F0.imprint","IMPRINT",EDGE,{"derivedFrom":subQ0}),1.0]])]});}
            extrude(context, id + "F18", {"entities" : qUnion([Q0, Q1, Q2, Q3, Q4]), "depth" : 70 * mm});
        }
        {
            var Q0;
            Q0=makeQuery(id+"F0.imprint","IMPRINT",FACE,{"disambiguationData":[TD([[makeQuery(id+"F0.imprint","IMPRINT",EDGE,{"derivedFrom":sQuery(id+"F0.wireOp",EDGE,"E32.1.0")}),-1.0]])]});
            var Q1;
            Q1=makeQuery(id+"F0.imprint","IMPRINT",FACE,{"disambiguationData":[TD([[makeQuery(id+"F0.imprint","IMPRINT",EDGE,{"derivedFrom":sQuery(id+"F0.wireOp",EDGE,"E32.1.1")}),-1.0]])]});
            extrude(context, id + "F19", {"entities" : qUnion([Q0, Q1]), "depth" : 10 * mm});
        }
        {
            var Q0;
            Q0=makeQuery(id+"F0.imprint","IMPRINT",FACE,{"disambiguationData":[TD([[makeQuery(id+"F0.imprint","IMPRINT",EDGE,{"derivedFrom":sQuery(id+"F0.wireOp",EDGE,"E32.1.0")}),1.0]])]});
            var Q1;
            Q1=makeQuery(id+"F0.imprint","IMPRINT",FACE,{"disambiguationData":[TD([[makeQuery(id+"F0.imprint","IMPRINT",EDGE,{"derivedFrom":sQuery(id+"F0.wireOp",EDGE,"E32.1.2")}),-1.0]])]});
            var Q2;
            Q2=makeQuery(id+"F0.imprint","IMPRINT",FACE,{"disambiguationData":[TD([[makeQuery(id+"F0.imprint","IMPRINT",EDGE,{"derivedFrom":sQuery(id+"F0.wireOp",EDGE,"E32.1.3")}),-1.0]])]});
            var Q3;
            Q3=makeQuery(id+"F0.imprint","IMPRINT",FACE,{"disambiguationData":[TD([[makeQuery(id+"F0.imprint","IMPRINT",EDGE,{"derivedFrom":sQuery(id+"F0.wireOp",EDGE,"E32.1.1")}),1.0]])]});
            extrude(context, id + "F20", {"entities" : qUnion([Q0, Q1, Q2, Q3]), "depth" : 70 * mm});
        }
        {
            var Q0;
            Q0=makeQuery(id+"F20.opExtrude","SWEPT_FACE",FACE,{"disambiguationData":[OSD([sQuery(id+"F0.wireOp",EDGE,"E32.1.12")])]});
            var sketch = newSketch(context, id + "F21", { "sketchPlane" : qUnion([Q0])});
            skLineSegment(sketch, "E85.0", {"start": v(92.5, 70) * mm, "end": v(92.5, 0) * mm, "construction": true});
            skPoint(sketch, "E86", {"position": v(92.5, 55) * mm});
            skPoint(sketch, "E87", {"position": v(92.5, 25) * mm});
            skSolve(sketch);
        }
        {
            var Q0;
            Q0=makeQuery(id+"F20.opExtrude","SWEPT_FACE",FACE,{"disambiguationData":[OSD([sQuery(id+"F0.wireOp",EDGE,"E32.1.3")])]});
            var sketch = newSketch(context, id + "F22", { "sketchPlane" : qUnion([Q0])});
            skLineSegment(sketch, "E88.0", {"start": v(-92.5, 70) * mm, "end": v(-92.5, 0) * mm, "construction": true});
            skPoint(sketch, "E89", {"position": v(-92.5, 55) * mm});
            skPoint(sketch, "E90", {"position": v(-92.5, 25) * mm});
            skSolve(sketch);
        }
        {
            var Q0;
            Q0=sQuery(id+"F21.wireOp",VERTEX,"E86");
            var Q1;
            Q1=sQuery(id+"F21.wireOp",VERTEX,"E87");
            var Q2;
            Q2=sQuery(id+"F22.wireOp",VERTEX,"E89");
            var Q3;
            Q3=sQuery(id+"F22.wireOp",VERTEX,"E90");
            var Q4;
            Q4=makeQuery(id+"F20.opExtrude","SWEPT_BODY",BODY,{"disambiguationData":[OSD([sQuery(id+"F0.wireOp",EDGE,"E32.1.0"),sQuery(id+"F0.wireOp",EDGE,"E32.1.1"),sQuery(id+"F0.wireOp",EDGE,"E32.1.3"),sQuery(id+"F0.wireOp",EDGE,"E32.1.5"),sQuery(id+"F0.wireOp",EDGE,"E32.1.7"),sQuery(id+"F0.wireOp",EDGE,"E32.1.9"),sQuery(id+"F0.wireOp",EDGE,"E32.1.10"),sQuery(id+"F0.wireOp",EDGE,"E32.1.11"),sQuery(id+"F0.wireOp",EDGE,"E32.1.12"),sQuery(id+"F0.wireOp",EDGE,"E32.1.15"),sQuery(id+"F0.wireOp",EDGE,"E32.1.17"),sQuery(id+"F0.wireOp",EDGE,"E32.1.20")])]});
            hole(context, id + "F23", {"style" : HoleStyle.C_BORE, "holeDiameter" : 6 * mm, "cBoreDiameter" : 11 * mm, "cBoreDepth" : 5 * mm, "endStyle" : HoleEndStyle.THROUGH, "locations" : qUnion([Q0, Q1, Q2, Q3]), "scope" : qUnion([Q4])});
        }
        {
            var Q0;
            Q0=sQuery(id+"F0.wireOp",VERTEX,"E45");
            var Q1;
            Q1=sQuery(id+"F0.wireOp",VERTEX,"E46");
            var Q2;
            Q2=makeQuery(id+"F19.opExtrude","SWEPT_BODY",BODY,{"disambiguationData":[OSD([sQuery(id+"F0.wireOp",EDGE,"E32.1.1"),sQuery(id+"F0.wireOp",EDGE,"E32.1.13"),sQuery(id+"F0.wireOp",EDGE,"E32.1.16"),sQuery(id+"F0.wireOp",EDGE,"E32.1.17")])]});
            var Q3;
            Q3=makeQuery(id+"F19.opExtrude","SWEPT_BODY",BODY,{"disambiguationData":[OSD([sQuery(id+"F0.wireOp",EDGE,"E32.1.0"),sQuery(id+"F0.wireOp",EDGE,"E32.1.6"),sQuery(id+"F0.wireOp",EDGE,"E32.1.8"),sQuery(id+"F0.wireOp",EDGE,"E32.1.10")])]});
            hole(context, id + "F24", {"style" : HoleStyle.C_BORE, "holeDiameter" : 8 * mm, "cBoreDiameter" : 14 * mm, "cBoreDepth" : 6 * mm, "endStyle" : HoleEndStyle.THROUGH, "oppositeDirection" : true, "locations" : qUnion([Q0, Q1]), "scope" : qUnion([Q2, Q3])});
        }
        {
            var Q0;
            Q0=sQuery(id+"F0.wireOp",VERTEX,"E49");
            var Q1;
            Q1=sQuery(id+"F0.wireOp",VERTEX,"E50");
            var Q2;
            Q2=makeQuery(id+"F17.opExtrude","SWEPT_BODY",BODY,{"disambiguationData":[OSD([sQuery(id+"F0.wireOp",EDGE,"E32.2.0"),sQuery(id+"F0.wireOp",EDGE,"E32.2.6"),sQuery(id+"F0.wireOp",EDGE,"E32.2.8"),sQuery(id+"F0.wireOp",EDGE,"E32.2.10")])]});
            var Q3;
            Q3=makeQuery(id+"F17.opExtrude","SWEPT_BODY",BODY,{"disambiguationData":[OSD([sQuery(id+"F0.wireOp",EDGE,"E32.2.1"),sQuery(id+"F0.wireOp",EDGE,"E32.2.13"),sQuery(id+"F0.wireOp",EDGE,"E32.2.16"),sQuery(id+"F0.wireOp",EDGE,"E32.2.17")])]});
            hole(context, id + "F25", {"style" : HoleStyle.C_BORE, "holeDiameter" : 8 * mm, "cBoreDiameter" : 14 * mm, "cBoreDepth" : 6 * mm, "endStyle" : HoleEndStyle.THROUGH, "oppositeDirection" : true, "locations" : qUnion([Q0, Q1]), "scope" : qUnion([Q2, Q3])});
        }
    });
